# Revit family: FONESTAR_Proyector_Sonido_Exterior_Bidireccional
name_source: partatom
category: Communication Devices
units: mm (PartAtom-declared; Revit-internal decimal feet)

## family parameters
Always vertical = No
Cut with Voids When Loaded = No
Maintain Annotation Orientation = No
Part Type = Normal
Room Calculation Point = No
Round Connector Dimension = Use Diameter
Shared = No
Work Plane-Based = Yes

## types (1)
- PF-25TD
    Altura = 150 mm
    Cuerpo.Longitud = 146 mm  [stored 0.479003 ft]
    Cuerpo.Material = Plástico ABS - Blanco RAL(9016)
    Default Elevation = 1000 mm  [stored 3.28084 ft]
    Description = Proyector de sonido bidireccional con transformador de línea 100 V.
    Diámetro = 138 mm  [stored 0.452756 ft]
    Embellecedor.Espesor = 2 mm  [stored 0.00656168 ft]
    Frontal.Longitud = 20 mm  [stored 0.0656168 ft]
    Lente.Espesor = 5 mm  [stored 0.0164042 ft]
    Longitud = 200 mm  [stored 0.656168 ft]
    Manufacturer = FONESTAR
    Model = PF-25TD
    Modified by = XPV
    Peso = 1,7 Kg
    Potencia Acústica = 10 W
    Protección IP = IP-55
    Rejilla.Curva.Espesor = 1 mm  [stored 0.00328084 ft]
    Rejilla.Desfase = 7 mm  [stored 0.0229659 ft]
    Rejilla.Espesor = 2 mm  [stored 0.00656168 ft]
    Rejilla.Material = Aluminio_Rejilla - Blanco RAL(9016)
    Respuesta Acústica = 130-15.000 Hz
    Reviewed by = TAG
    Soporte.Altura = 165 mm
    Soporte.Espesor = 3 mm  [stored 0.00984252 ft]
    Soporte.Longitud = 30 mm  [stored 0.0984252 ft]
    Soporte.Material = Plástico ABS - Blanco RAL(9016)
    URL = https://fonestar.com
    URL.Product = https://fonestar.com
    Version = R0

note: [stored X ft] marks values corroborated as IEEE doubles in the binary element streams (Revit-internal decimal feet)
